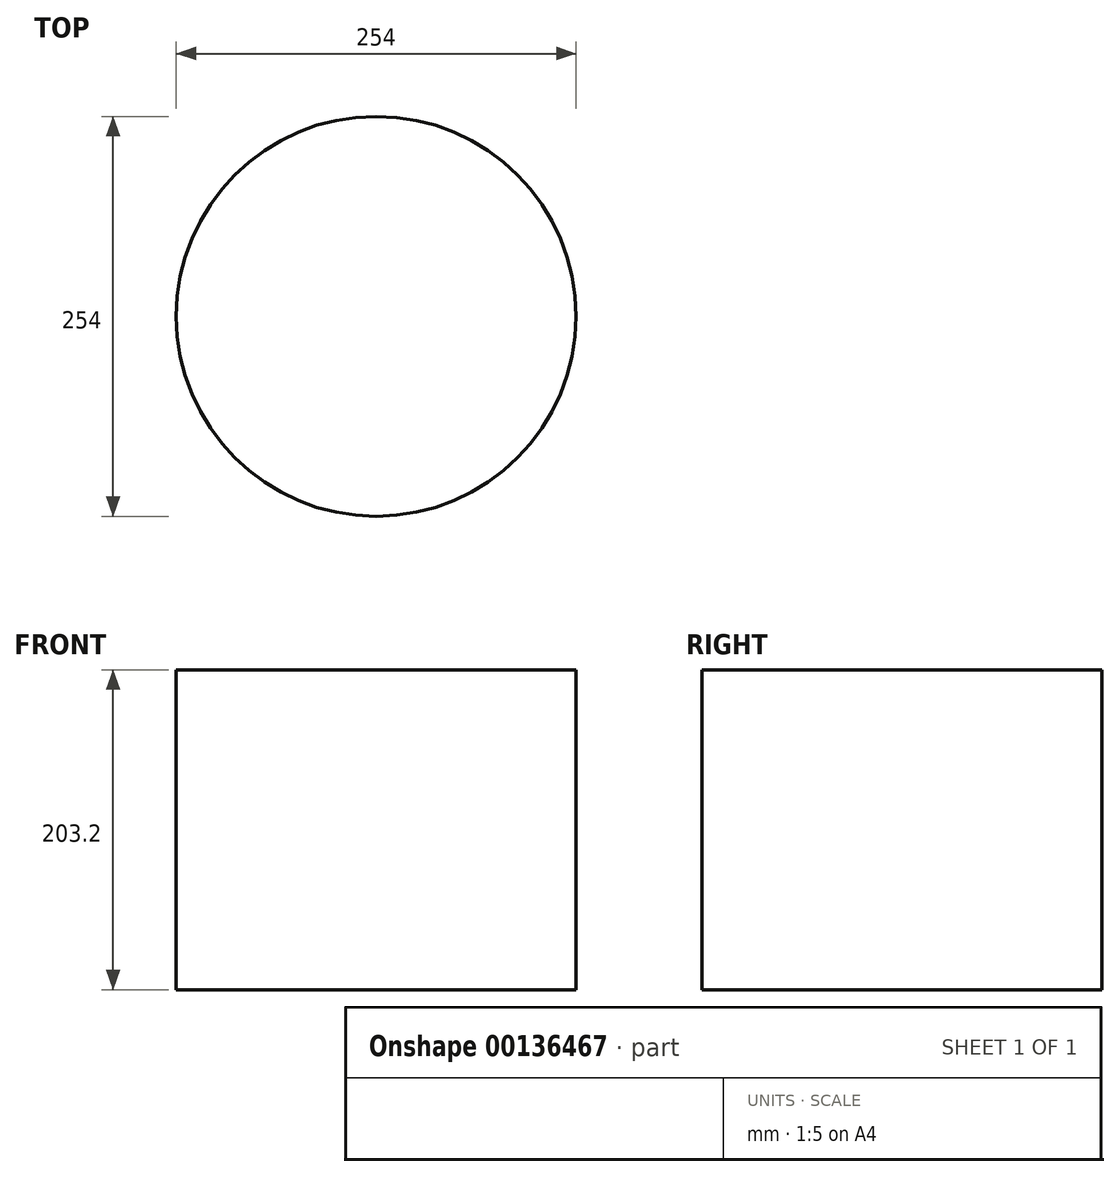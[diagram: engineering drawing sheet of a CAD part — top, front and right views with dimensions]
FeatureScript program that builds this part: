
annotation { "Feature Type Name" : "Feature", "Feature Type Description" : "" }
export const myFeature = defineFeature(function(context is Context, id is Id, definition is map)
    precondition{}
    {
        {
            var Q0;
            Q0=qCreatedBy(makeId("Top.planeOp"),FACE);
            var sketch = newSketch(context, id + "F0", { "sketchPlane" : qUnion([Q0])});
            skCircle(sketch, "E0", {"center": v(0, 0) * mm, "radius": 127 * mm});
            skSolve(sketch);
        }
        {
            var Q0;
            Q0=makeQuery(id+"F0.imprint","IMPRINT",FACE,{"disambiguationData":[TD([[makeQuery(id+"F0.imprint","IMPRINT",EDGE,{"derivedFrom":sQuery(id+"F0.wireOp",EDGE,"E0")}),1.0]])]});
            extrude(context, id + "F1", {"entities" : qUnion([Q0]), "depth" : 203.2 * mm});
        }
    });
